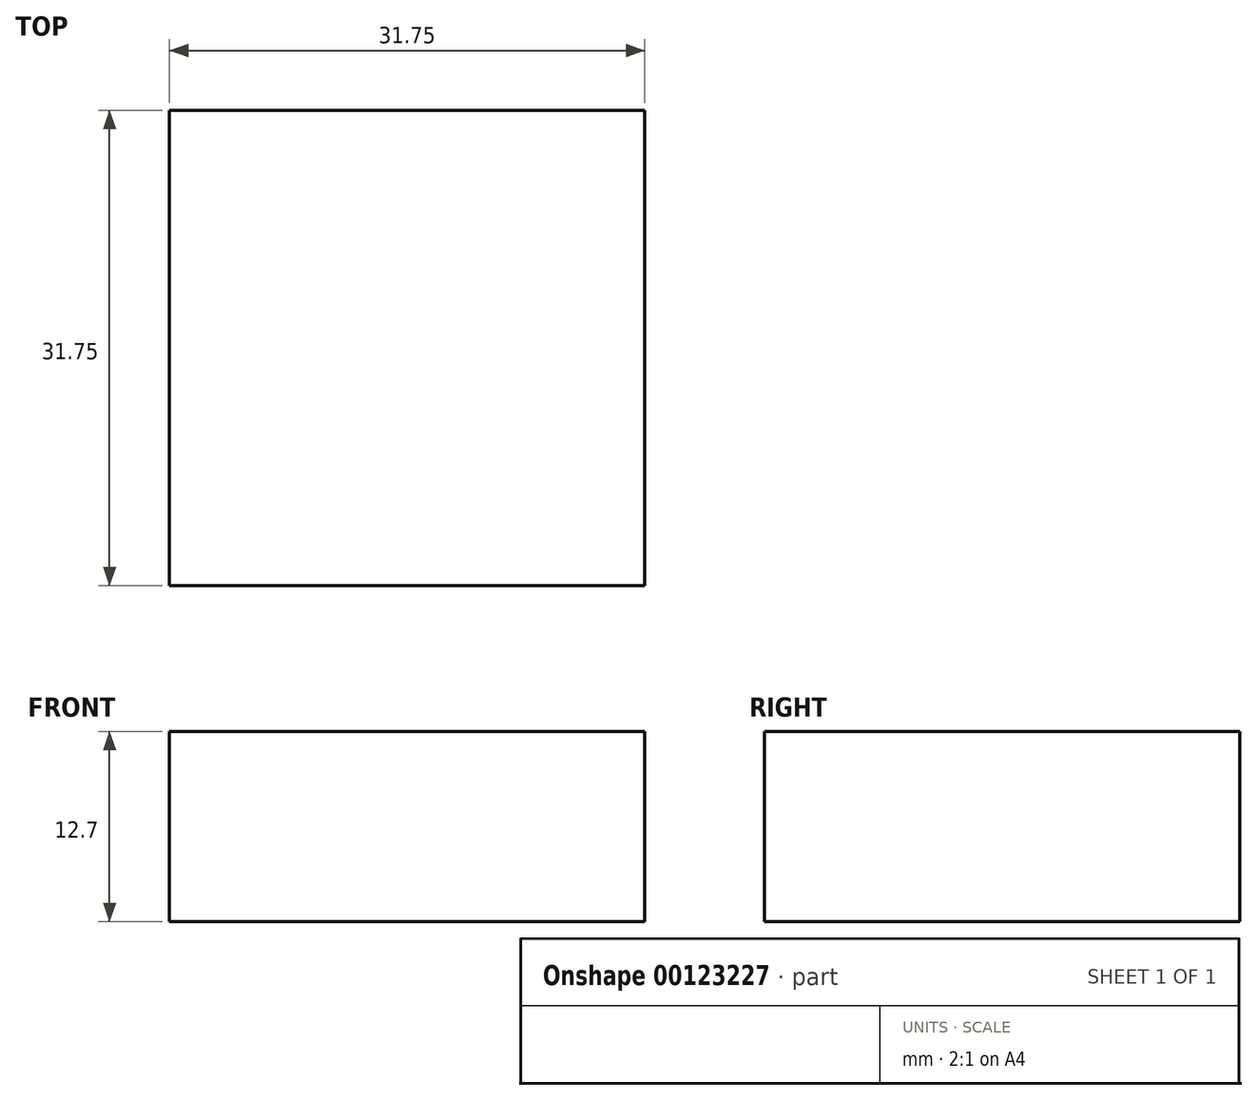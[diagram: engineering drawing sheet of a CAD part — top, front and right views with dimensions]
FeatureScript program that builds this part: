
annotation { "Feature Type Name" : "Feature", "Feature Type Description" : "" }
export const myFeature = defineFeature(function(context is Context, id is Id, definition is map)
    precondition{}
    {
        {
            var Q0;
            Q0=qCreatedBy(makeId("Top.planeOp"),FACE);
            var sketch = newSketch(context, id + "F0", { "sketchPlane" : qUnion([Q0])});
            skLineSegment(sketch, "E0.bottom", {"start": v(-13.72, 31.75) * mm, "end": v(18.03, 31.75) * mm});
            skLineSegment(sketch, "E0.top", {"start": v(-13.72, 0) * mm, "end": v(18.03, 0) * mm});
            skLineSegment(sketch, "E0.left", {"start": v(-13.72, 31.75) * mm, "end": v(-13.72, 0) * mm});
            skLineSegment(sketch, "E0.right", {"start": v(18.03, 31.75) * mm, "end": v(18.03, 0) * mm});
            skSolve(sketch);
        }
        {
            var Q0;
            Q0=makeQuery(id+"F0.imprint","IMPRINT",FACE,{"disambiguationData":[TD([[makeQuery(id+"F0.imprint","IMPRINT",EDGE,{"derivedFrom":sQuery(id+"F0.wireOp",EDGE,"E0.bottom")}),-1.0]])]});
            extrude(context, id + "F1", {"entities" : qUnion([Q0]), "depth" : 12.7 * mm});
        }
    });
